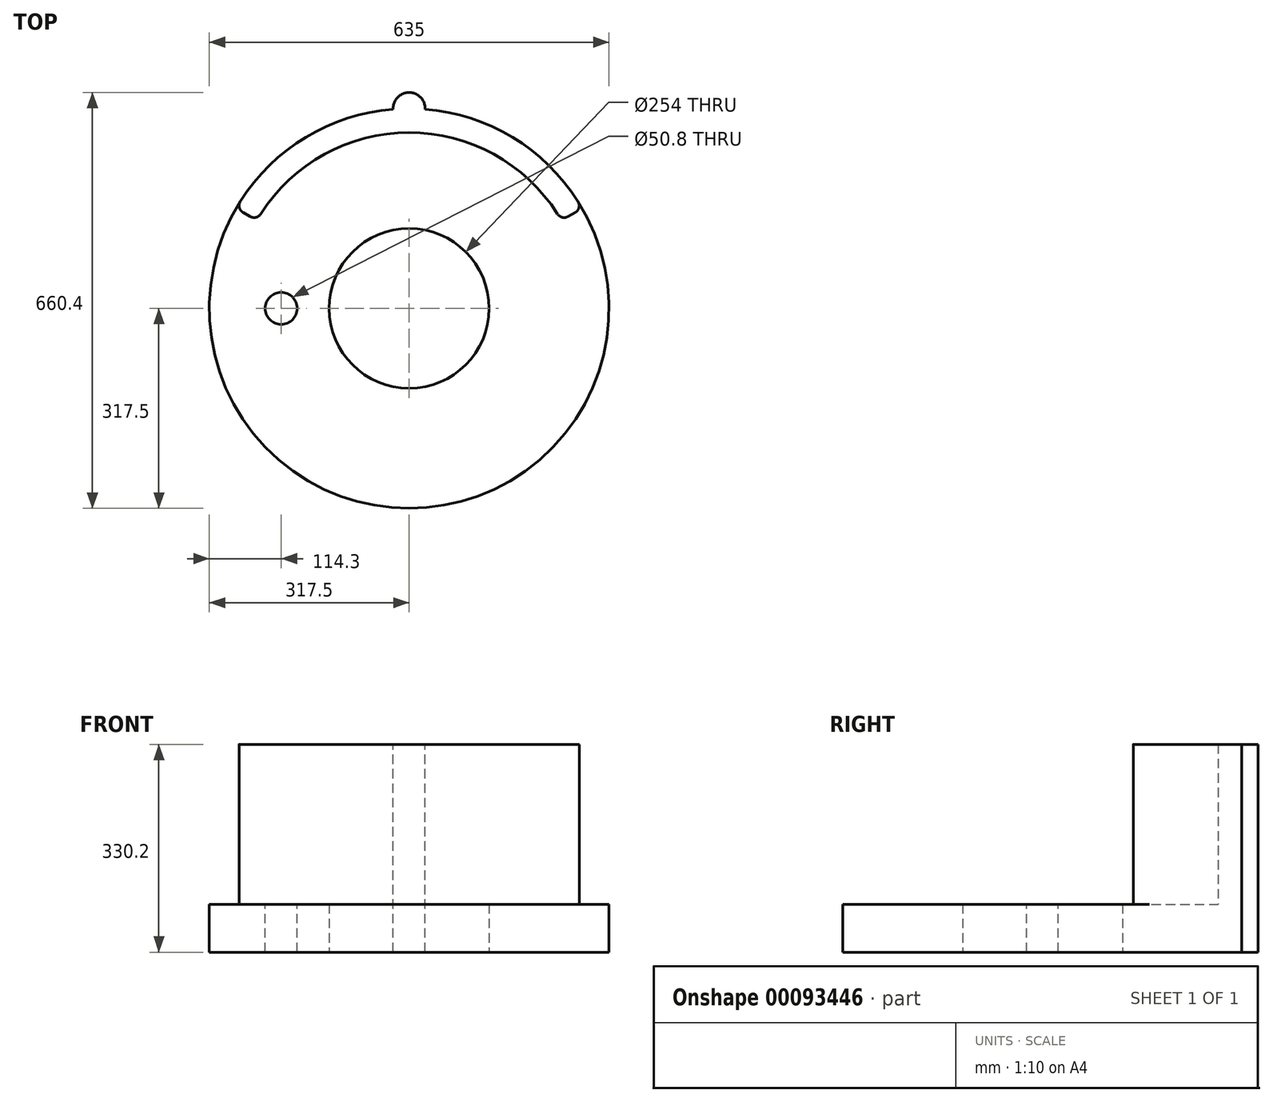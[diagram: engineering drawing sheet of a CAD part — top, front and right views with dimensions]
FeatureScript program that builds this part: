
annotation { "Feature Type Name" : "Feature", "Feature Type Description" : "" }
export const myFeature = defineFeature(function(context is Context, id is Id, definition is map)
    precondition{}
    {
        {
            var Q0;
            Q0=qCreatedBy(makeId("Top.planeOp"),FACE);
            var sketch = newSketch(context, id + "F0", { "sketchPlane" : qUnion([Q0])});
            skCircle(sketch, "E0", {"center": v(0, 0) * mm, "radius": 317.5 * mm});
            skCircle(sketch, "E1", {"center": v(0, 0) * mm, "radius": 127 * mm});
            skSolve(sketch);
        }
        {
            var Q0;
            Q0 = qSketchRegion(id + "F0", true);
            extrude(context, id + "F1", {"entities" : qUnion([Q0]), "depth" : 76.2 * mm});
        }
        {
            var Q0;
            Q0=makeQuery(id+"F1.opExtrude","CAP_FACE",FACE,{"disambiguationData":[OSD([sQuery(id+"F0.wireOp",EDGE,"E0"),sQuery(id+"F0.wireOp",EDGE,"E1")])],"isStart":false});
            var sketch = newSketch(context, id + "F2", { "sketchPlane" : qUnion([Q0])});
            skCircle(sketch, "E2", {"center": v(0, 0) * mm, "radius": 279.4 * mm});
            skLineSegment(sketch, "E3", {"start": v(0, 0) * mm, "end": v(-274.96, 158.75) * mm});
            skLineSegment(sketch, "E4", {"start": v(0, 0) * mm, "end": v(274.96, 158.75) * mm});
            skSolve(sketch);
        }
        {
            var Q0;
            {var subQ0=sQuery(id+"F2.wireOp",EDGE,"E3");var subQ1=sQuery(id+"F2.wireOp",EDGE,"E2");var subQ2=makeQuery(id+"F2.imprint","INTERSECT",VERTEX,{"derivedFrom":[subQ1,subQ0]});Q0=makeQuery(id+"F2.imprint","IMPRINT",FACE,{"disambiguationData":[TD([[makeQuery(id+"F2.imprint","IMPRINT",EDGE,{"disambiguationData":[TD([[subQ2,1.0]])],"derivedFrom":subQ1}),-1.0]])]});}
            extrude(context, id + "F3", {"entities" : qUnion([Q0]), "operationType" : NewBodyOperationType.ADD, "depth" : 254 * mm});
        }
        {
            var Q0;
            Q0=makeQuery(id+"F3.opExtrude","SWEPT_EDGE",EDGE,{"disambiguationData":[OSD([sQuery(id+"F0.wireOp",EDGE,"E0"),sQuery(id+"F2.wireOp",EDGE,"E3")])]});
            var Q1;
            Q1=makeQuery(id+"F3.opExtrude","SWEPT_EDGE",EDGE,{"disambiguationData":[OSD([sQuery(id+"F2.wireOp",EDGE,"E2"),sQuery(id+"F2.wireOp",EDGE,"E3")])]});
            var Q2;
            Q2=makeQuery(id+"F3.opExtrude","SWEPT_EDGE",EDGE,{"disambiguationData":[OSD([sQuery(id+"F2.wireOp",EDGE,"E2"),sQuery(id+"F2.wireOp",EDGE,"E4")])]});
            var Q3;
            Q3=makeQuery(id+"F3.opExtrude","SWEPT_EDGE",EDGE,{"disambiguationData":[OSD([sQuery(id+"F0.wireOp",EDGE,"E0"),sQuery(id+"F2.wireOp",EDGE,"E4")])]});
            fillet(context, id + "F4", {"entities" : qUnion([Q0, Q1, Q2, Q3]), "radius" : 12.7 * mm, "tangentPropagation" : true, "allowEdgeOverflow" : false});
        }
        {
            var Q0;
            Q0=makeQuery(id+"F3.opExtrude","CAP_FACE",FACE,{"disambiguationData":[OSD([sQuery(id+"F0.wireOp",EDGE,"E0"),sQuery(id+"F2.wireOp",EDGE,"E2"),sQuery(id+"F2.wireOp",EDGE,"E3"),sQuery(id+"F2.wireOp",EDGE,"E4")])],"isStart":false});
            var sketch = newSketch(context, id + "F5", { "sketchPlane" : qUnion([Q0])});
            skCircle(sketch, "E5", {"center": v(0, 317.5) * mm, "radius": 25.4 * mm});
            skSolve(sketch);
        }
        {
            var Q0;
            {var subQ0=sQuery(id+"F5.wireOp",EDGE,"E5");var subQ1=makeQuery(id+"F3.opExtrude","CAP_EDGE",EDGE,{"disambiguationData":[OSD([sQuery(id+"F0.wireOp",EDGE,"E0")])],"isStart":false});var subQ2=makeQuery(id+"F5.imprint","INTERSECT",VERTEX,{"disambiguationData":[OD(0.0)],"derivedFrom":[subQ1,subQ0]});Q0=makeQuery(id+"F5.imprint","IMPRINT",FACE,{"disambiguationData":[TD([[makeQuery(id+"F5.imprint","IMPRINT",EDGE,{"disambiguationData":[TD([[subQ2,1.0]])],"derivedFrom":subQ0}),1.0]])]});}
            var Q1;
            Q1=makeQuery(id+"F1.opExtrude","CAP_FACE",FACE,{"disambiguationData":[OSD([sQuery(id+"F0.wireOp",EDGE,"E0"),sQuery(id+"F0.wireOp",EDGE,"E1")])],"isStart":true});
            extrude(context, id + "F6", {"entities" : qUnion([Q0]), "operationType" : NewBodyOperationType.ADD, "endBound" : BoundingType.UP_TO_SURFACE, "oppositeDirection" : true, "endBoundEntityFace" : qUnion([Q1]), "depth" : 25.4 * mm});
        }
        {
            var Q0;
            Q0=makeQuery(id+"F1.opExtrude","CAP_FACE",FACE,{"disambiguationData":[OSD([sQuery(id+"F0.wireOp",EDGE,"E0"),sQuery(id+"F0.wireOp",EDGE,"E1")])],"isStart":false});
            var sketch = newSketch(context, id + "F7", { "sketchPlane" : qUnion([Q0])});
            skCircle(sketch, "E6", {"center": v(-203.2, 0) * mm, "radius": 25.4 * mm});
            skSolve(sketch);
        }
        {
            var Q0;
            Q0=makeQuery(id+"F7.imprint","IMPRINT",FACE,{"disambiguationData":[TD([[makeQuery(id+"F7.imprint","IMPRINT",EDGE,{"derivedFrom":sQuery(id+"F7.wireOp",EDGE,"E6")}),1.0]])]});
            extrude(context, id + "F8", {"entities" : qUnion([Q0]), "operationType" : NewBodyOperationType.REMOVE, "endBound" : BoundingType.THROUGH_ALL, "oppositeDirection" : true, "depth" : 25.4 * mm});
        }
    });
